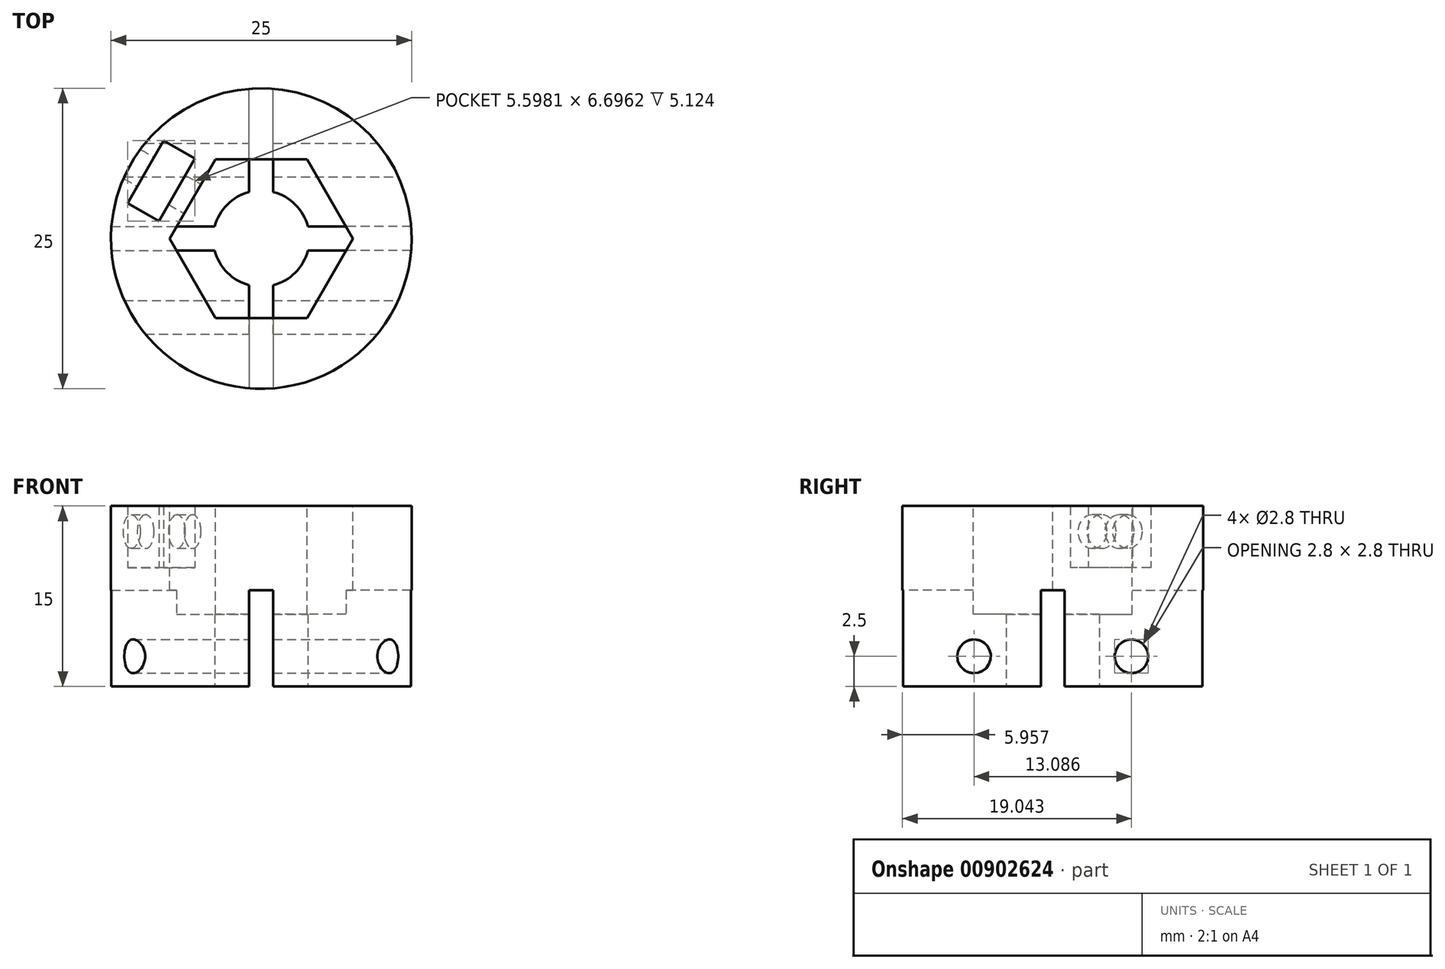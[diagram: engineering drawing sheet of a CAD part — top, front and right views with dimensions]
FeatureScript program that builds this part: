
annotation { "Feature Type Name" : "Feature", "Feature Type Description" : "" }
export const myFeature = defineFeature(function(context is Context, id is Id, definition is map)
    precondition{}
    {
        {
            var Q0;
            Q0=qCreatedBy(makeId("Top.planeOp"),FACE);
            var sketch = newSketch(context, id + "F0", { "sketchPlane" : qUnion([Q0])});
            skCircle(sketch, "E0", {"center": v(0, 0) * mm, "radius": 12.5 * mm});
            skSolve(sketch);
        }
        {
            var Q0;
            Q0 = qSketchRegion(id + "F0", true);
            extrude(context, id + "F1", {"entities" : qUnion([Q0]), "depth" : 15 * mm, "offsetDistance" : 25 * mm});
        }
        {
            var Q0;
            Q0=makeQuery(id+"F1.opExtrude","CAP_FACE",FACE,{"disambiguationData":[OSD([sQuery(id+"F0.wireOp",EDGE,"E0")])],"isStart":true});
            var sketch = newSketch(context, id + "F2", { "sketchPlane" : qUnion([Q0])});
            skLineSegment(sketch, "E1", {"start": v(-12.5, 1) * mm, "end": v(-3.87, 1) * mm});
            skPoint(sketch, "E2", {"position": v(-12.5, 0) * mm});
            skPoint(sketch, "E3", {"position": v(0, 12.5) * mm});
            skLineSegment(sketch, "E4.MirrorCS", {"start": v(12.5, 1) * mm, "end": v(3.87, 1) * mm});
            skLineSegment(sketch, "E5.MirrorCS", {"start": v(-12.5, -1) * mm, "end": v(-3.87, -1) * mm});
            skLineSegment(sketch, "E6.MirrorCS", {"start": v(12.5, -1) * mm, "end": v(3.87, -1) * mm});
            skLineSegment(sketch, "E7", {"start": v(-12.5, 1) * mm, "end": v(-12.5, -1) * mm});
            skLineSegment(sketch, "E8", {"start": v(12.5, 1) * mm, "end": v(12.5, -1) * mm});
            skLineSegment(sketch, "E9", {"start": v(1, 12.5) * mm, "end": v(-1, 12.5) * mm});
            skLineSegment(sketch, "E10", {"start": v(1, -12.5) * mm, "end": v(-1, -12.5) * mm});
            skLineSegment(sketch, "E11", {"start": v(-1, -3.87) * mm, "end": v(-1, -12.5) * mm});
            skArc(sketch, "E12", {"start": v(-1, 3.87) * mm, "mid": v(-2.83, 2.83) * mm, "end": v(-3.87, 1) * mm});
            skArc(sketch, "E13", {"start": v(3.87, 1) * mm, "mid": v(2.83, 2.83) * mm, "end": v(1, 3.87) * mm});
            skArc(sketch, "E14", {"start": v(1, -3.87) * mm, "mid": v(2.83, -2.83) * mm, "end": v(3.87, -1) * mm});
            skLineSegment(sketch, "E15", {"start": v(1, -3.87) * mm, "end": v(1, -12.5) * mm});
            skLineSegment(sketch, "E16", {"start": v(-1, 3.87) * mm, "end": v(-1, 12.5) * mm});
            skLineSegment(sketch, "E17", {"start": v(1, 3.87) * mm, "end": v(1, 12.5) * mm});
            skPoint(sketch, "E18.MirrorCS.start.orphan", {"position": v(-1, -1) * mm});
            skPoint(sketch, "E19.MirrorCS.start.orphan", {"position": v(1, -1) * mm});
            skPoint(sketch, "E20.end.orphan", {"position": v(1, 1) * mm});
            skPoint(sketch, "E21.end.orphan", {"position": v(-1, 1) * mm});
            skArc(sketch, "E22.trimOffspring", {"start": v(-3.87, -1) * mm, "mid": v(-2.83, -2.83) * mm, "end": v(-1, -3.87) * mm});
            skSolve(sketch);
        }
        {
            var Q0;
            Q0 = qSketchRegion(id + "F2", true);
            extrude(context, id + "F3", {"entities" : qUnion([Q0]), "operationType" : NewBodyOperationType.REMOVE, "oppositeDirection" : true, "depth" : 8 * mm, "offsetDistance" : 25 * mm});
        }
        {
            var Q0;
            Q0=makeQuery(id+"F1.opExtrude","CAP_FACE",FACE,{"disambiguationData":[OSD([sQuery(id+"F0.wireOp",EDGE,"E0")])],"isStart":false});
            var sketch = newSketch(context, id + "F4", { "sketchPlane" : qUnion([Q0])});
            skCircle(sketch, "E23.cCircle", {"center": v(0, 0) * mm, "radius": 6.6 * mm, "construction": true});
            skLineSegment(sketch, "E23.0", {"start": v(-3.81, 6.6) * mm, "end": v(3.81, 6.6) * mm});
            skLineSegment(sketch, "E23.1", {"start": v(3.81, 6.6) * mm, "end": v(7.62, 0) * mm});
            skLineSegment(sketch, "E23.2", {"start": v(7.62, 0) * mm, "end": v(3.81, -6.6) * mm});
            skLineSegment(sketch, "E23.3", {"start": v(3.81, -6.6) * mm, "end": v(-3.81, -6.6) * mm});
            skLineSegment(sketch, "E23.4", {"start": v(-3.81, -6.6) * mm, "end": v(-7.62, 0) * mm});
            skLineSegment(sketch, "E23.5", {"start": v(-7.62, 0) * mm, "end": v(-3.81, 6.6) * mm});
            skPoint(sketch, "E23.0.midPoint", {"position": v(0, 6.6) * mm});
            skSolve(sketch);
        }
        {
            var Q0;
            Q0=makeQuery(id+"F4.imprint","IMPRINT",FACE,{"disambiguationData":[TD([[makeQuery(id+"F4.imprint","IMPRINT",EDGE,{"derivedFrom":sQuery(id+"F4.wireOp",EDGE,"E23.0")}),-1.0]])]});
            extrude(context, id + "F5", {"entities" : qUnion([Q0]), "operationType" : NewBodyOperationType.REMOVE, "oppositeDirection" : true, "depth" : 9 * mm, "offsetDistance" : 25 * mm});
        }
        {
            var Q0;
            Q0=makeQuery(id+"F5.boolean.opBoolean","COPY",FACE,{"derivedFrom":makeQuery(id+"F5.opExtrude","SWEPT_FACE",FACE,{"disambiguationData":[OSD([sQuery(id+"F4.wireOp",EDGE,"E23.5")])]})});
            var sketch = newSketch(context, id + "F6", { "sketchPlane" : qUnion([Q0])});
            skCircle(sketch, "E24", {"center": v(0, 12.88) * mm, "radius": 1.4 * mm});
            skPoint(sketch, "E25", {"position": v(0, 15) * mm});
            skSolve(sketch);
        }
        {
            var Q0;
            Q0 = qSketchRegion(id + "F6", true);
            extrude(context, id + "F7", {"entities" : qUnion([Q0]), "operationType" : NewBodyOperationType.REMOVE, "endBound" : BoundingType.UP_TO_NEXT, "oppositeDirection" : true, "depth" : 25 * mm, "offsetDistance" : 25 * mm});
        }
        {
            var Q0;
            Q0=makeQuery(id+"F5.boolean.opBoolean","COPY",FACE,{"derivedFrom":makeQuery(id+"F5.opExtrude","SWEPT_FACE",FACE,{"disambiguationData":[OSD([sQuery(id+"F4.wireOp",EDGE,"E23.5")])]})});
            cPlane(context, id + "F8", {"entities" : qUnion([Q0]), "cplaneType" : CPlaneType.OFFSET, "offset" : 1.5 * mm, "oppositeDirection" : true, "width" : 150 * mm, "height" : 150 * mm});
        }
        {
            var Q0;
            Q0=qCreatedBy(id+"F8.planeOp",FACE);
            var sketch = newSketch(context, id + "F9", { "sketchPlane" : qUnion([Q0])});
            skCircle(sketch, "E26.0", {"center": v(0, 12.88) * mm, "radius": 1.4 * mm, "construction": true});
            skLineSegment(sketch, "E27.bottom", {"start": v(3, 15.88) * mm, "end": v(-3, 15.88) * mm});
            skLineSegment(sketch, "E27.top", {"start": v(3, 9.88) * mm, "end": v(-3, 9.88) * mm});
            skLineSegment(sketch, "E27.left", {"start": v(3, 15.88) * mm, "end": v(3, 9.88) * mm});
            skLineSegment(sketch, "E27.right", {"start": v(-3, 15.88) * mm, "end": v(-3, 9.88) * mm});
            skSolve(sketch);
        }
        {
            var Q0;
            Q0 = qSketchRegion(id + "F9", true);
            extrude(context, id + "F10", {"entities" : qUnion([Q0]), "operationType" : NewBodyOperationType.REMOVE, "oppositeDirection" : true, "depth" : 3 * mm, "offsetDistance" : 25 * mm});
        }
        {
            var Q0;
            Q0=qCreatedBy(makeId("Right.planeOp"),FACE);
            var sketch = newSketch(context, id + "F11", { "sketchPlane" : qUnion([Q0])});
            skCircle(sketch, "E28", {"center": v(6.54, 2.5) * mm, "radius": 1.4 * mm});
            skLineSegment(sketch, "E29.0", {"start": v(0.6, 5) * mm, "end": v(12.49, 5) * mm, "construction": true});
            skLineSegment(sketch, "E30.0", {"start": v(1, 0) * mm, "end": v(1, 0) * mm});
            skLineSegment(sketch, "E31.0", {"start": v(1, 0) * mm, "end": v(1, 8) * mm, "construction": true});
            skLineSegment(sketch, "E32.0", {"start": v(-1, 0) * mm, "end": v(-1, 5) * mm, "construction": true});
            skPoint(sketch, "E33", {"position": v(-1, 2.5) * mm});
            skPoint(sketch, "E34", {"position": v(6.54, 5) * mm});
            skCircle(sketch, "E35.MirrorC", {"center": v(-6.54, 2.5) * mm, "radius": 1.4 * mm});
            skSolve(sketch);
        }
        {
            var Q0;
            Q0 = qSketchRegion(id + "F11", true);
            extrude(context, id + "F12", {"entities" : qUnion([Q0]), "operationType" : NewBodyOperationType.REMOVE, "endBound" : BoundingType.THROUGH_ALL, "oppositeDirection" : true, "depth" : 25 * mm, "offsetDistance" : 25 * mm, "hasSecondDirection" : true, "secondDirectionBound" : SecondDirectionBoundingType.THROUGH_ALL, "secondDirectionOppositeDirection" : false, "secondDirectionDepth" : 25 * mm});
        }
    });
